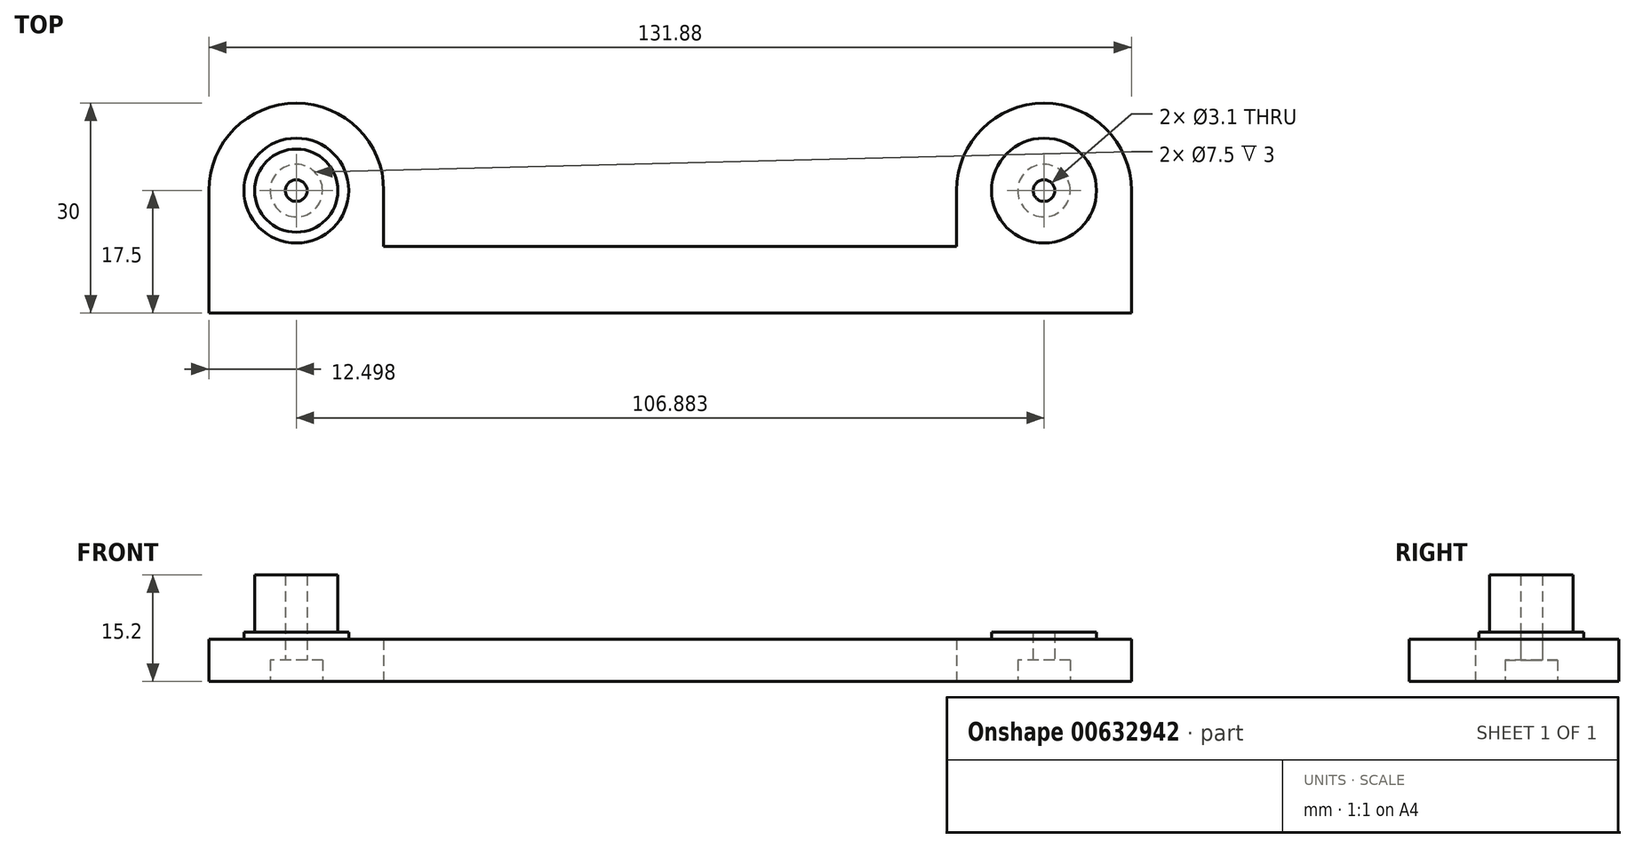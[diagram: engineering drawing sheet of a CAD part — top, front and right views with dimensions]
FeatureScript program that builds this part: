
annotation { "Feature Type Name" : "Feature", "Feature Type Description" : "" }
export const myFeature = defineFeature(function(context is Context, id is Id, definition is map)
    precondition{}
    {
        {
            var Q0;
            Q0=qCreatedBy(makeId("Top.planeOp"),FACE);
            var sketch = newSketch(context, id + "F0", { "sketchPlane" : qUnion([Q0])});
            skCircle(sketch, "E0", {"center": v(0, 0) * mm, "radius": 100 * mm, "construction": true});
            skCircle(sketch, "E1", {"center": v(-53.44, -95) * mm, "radius": 9 * mm, "construction": true});
            skLineSegment(sketch, "E2", {"start": v(0, 100) * mm, "end": v(0, -100) * mm, "construction": true});
            skLineSegment(sketch, "E3", {"start": v(0, -95) * mm, "end": v(-53.44, -95) * mm, "construction": true});
            skSolve(sketch);
        }
        {
            var Q0;
            Q0=qCreatedBy(makeId("Top.planeOp"),FACE);
            var sketch = newSketch(context, id + "F1", { "sketchPlane" : qUnion([Q0])});
            skCircle(sketch, "E4.0", {"center": v(-53.44, -95) * mm, "radius": 9 * mm, "construction": true});
            skArc(sketch, "E5", {"start": v(-40.94, -95) * mm, "mid": v(-53.44, -82.5) * mm, "end": v(-65.94, -95) * mm});
            skLineSegment(sketch, "E6", {"start": v(-65.94, -95) * mm, "end": v(-40.94, -95) * mm, "construction": true});
            skLineSegment(sketch, "E7", {"start": v(-65.94, -95) * mm, "end": v(-65.94, -112.5) * mm});
            skLineSegment(sketch, "E8", {"start": v(-65.94, -112.5) * mm, "end": v(0, -112.5) * mm});
            skLineSegment(sketch, "E9", {"start": v(-40.94, -95) * mm, "end": v(-40.94, -103) * mm});
            skLineSegment(sketch, "E10", {"start": v(-40.94, -103) * mm, "end": v(0, -103) * mm});
            skLineSegment(sketch, "E11.MirrorCS", {"start": v(40.94, -95) * mm, "end": v(40.94, -103) * mm});
            skLineSegment(sketch, "E12.MirrorCS", {"start": v(40.94, -103) * mm, "end": v(0, -103) * mm});
            skArc(sketch, "E13.MirrorCS", {"start": v(40.94, -95) * mm, "mid": v(53.44, -82.5) * mm, "end": v(65.94, -95) * mm});
            skLineSegment(sketch, "E14.MirrorCS", {"start": v(65.94, -112.5) * mm, "end": v(0, -112.5) * mm});
            skLineSegment(sketch, "E15.MirrorCS", {"start": v(65.94, -95) * mm, "end": v(65.94, -112.5) * mm});
            skCircle(sketch, "E16.MirrorC", {"center": v(53.44, -95) * mm, "radius": 9 * mm, "construction": true});
            skSolve(sketch);
        }
        {
            var Q0;
            Q0 = qSketchRegion(id + "F1", true);
            extrude(context, id + "F2", {"entities" : qUnion([Q0]), "depth" : 6 * mm, "offsetDistance" : 25 * mm});
        }
        {
            var Q0;
            Q0=makeQuery(id+"F2.opExtrude","CAP_FACE",FACE,{"disambiguationData":[OSD([sQuery(id+"F1.wireOp",EDGE,"E5"),sQuery(id+"F1.wireOp",EDGE,"E7"),sQuery(id+"F1.wireOp",EDGE,"E8"),sQuery(id+"F1.wireOp",EDGE,"E9"),sQuery(id+"F1.wireOp",EDGE,"E10"),sQuery(id+"F1.wireOp",EDGE,"E11.MirrorCS"),sQuery(id+"F1.wireOp",EDGE,"E12.MirrorCS"),sQuery(id+"F1.wireOp",EDGE,"E13.MirrorCS"),sQuery(id+"F1.wireOp",EDGE,"E14.MirrorCS"),sQuery(id+"F1.wireOp",EDGE,"E15.MirrorCS")])],"isStart":false});
            var sketch = newSketch(context, id + "F3", { "sketchPlane" : qUnion([Q0])});
            skCircle(sketch, "E17", {"center": v(-53.44, -95) * mm, "radius": 7.5 * mm});
            skCircle(sketch, "E18.MirrorC", {"center": v(53.44, -95) * mm, "radius": 7.5 * mm});
            skSolve(sketch);
        }
        {
            var Q0;
            Q0 = qSketchRegion(id + "F3", true);
            extrude(context, id + "F4", {"entities" : qUnion([Q0]), "operationType" : NewBodyOperationType.ADD, "depth" : 1 * mm, "offsetDistance" : 25 * mm});
        }
        {
            var Q0;
            Q0=makeQuery(id+"F4.opExtrude","CAP_FACE",FACE,{"disambiguationData":[OSD([sQuery(id+"F3.wireOp",EDGE,"E17")])],"isStart":false});
            var sketch = newSketch(context, id + "F5", { "sketchPlane" : qUnion([Q0])});
            skCircle(sketch, "E19", {"center": v(-53.44, -95) * mm, "radius": 5.95 * mm});
            skSolve(sketch);
        }
        {
            var Q0;
            Q0 = qSketchRegion(id + "F5", true);
            extrude(context, id + "F6", {"entities" : qUnion([Q0]), "operationType" : NewBodyOperationType.ADD, "depth" : 8.2 * mm, "offsetDistance" : 25 * mm});
        }
        {
            var Q0;
            Q0=makeQuery(id+"F1.imprint","IMPRINT",FACE,{"disambiguationData":[TD([[makeQuery(id+"F1.imprint","IMPRINT",EDGE,{"derivedFrom":sQuery(id+"F1.wireOp",EDGE,"E5")}),1.0]])]});
            var sketch = newSketch(context, id + "F7", { "sketchPlane" : qUnion([Q0])});
            skCircle(sketch, "E20.0", {"center": v(-53.44, -95) * mm, "radius": 9 * mm, "construction": true});
            skCircle(sketch, "E21", {"center": v(-53.44, -95) * mm, "radius": 1.55 * mm});
            skCircle(sketch, "E22.MirrorC", {"center": v(53.44, -95) * mm, "radius": 1.55 * mm});
            skSolve(sketch);
        }
        {
            var Q0;
            Q0 = qSketchRegion(id + "F7", true);
            extrude(context, id + "F8", {"entities" : qUnion([Q0]), "operationType" : NewBodyOperationType.REMOVE, "endBound" : BoundingType.THROUGH_ALL, "depth" : 25 * mm, "offsetDistance" : 25 * mm});
        }
        {
            var Q0;
            Q0=makeQuery(id+"F1.imprint","IMPRINT",FACE,{"disambiguationData":[TD([[makeQuery(id+"F1.imprint","IMPRINT",EDGE,{"derivedFrom":sQuery(id+"F1.wireOp",EDGE,"E5")}),1.0]])]});
            var sketch = newSketch(context, id + "F9", { "sketchPlane" : qUnion([Q0])});
            skCircle(sketch, "E23.0", {"center": v(-53.44, -95) * mm, "radius": 9 * mm, "construction": true});
            skCircle(sketch, "E24", {"center": v(-53.44, -95) * mm, "radius": 3.75 * mm});
            skCircle(sketch, "E25.MirrorC", {"center": v(53.44, -95) * mm, "radius": 3.75 * mm});
            skSolve(sketch);
        }
        {
            var Q0;
            Q0 = qSketchRegion(id + "F9", true);
            extrude(context, id + "F10", {"entities" : qUnion([Q0]), "operationType" : NewBodyOperationType.REMOVE, "depth" : 3 * mm, "offsetDistance" : 25 * mm});
        }
    });
